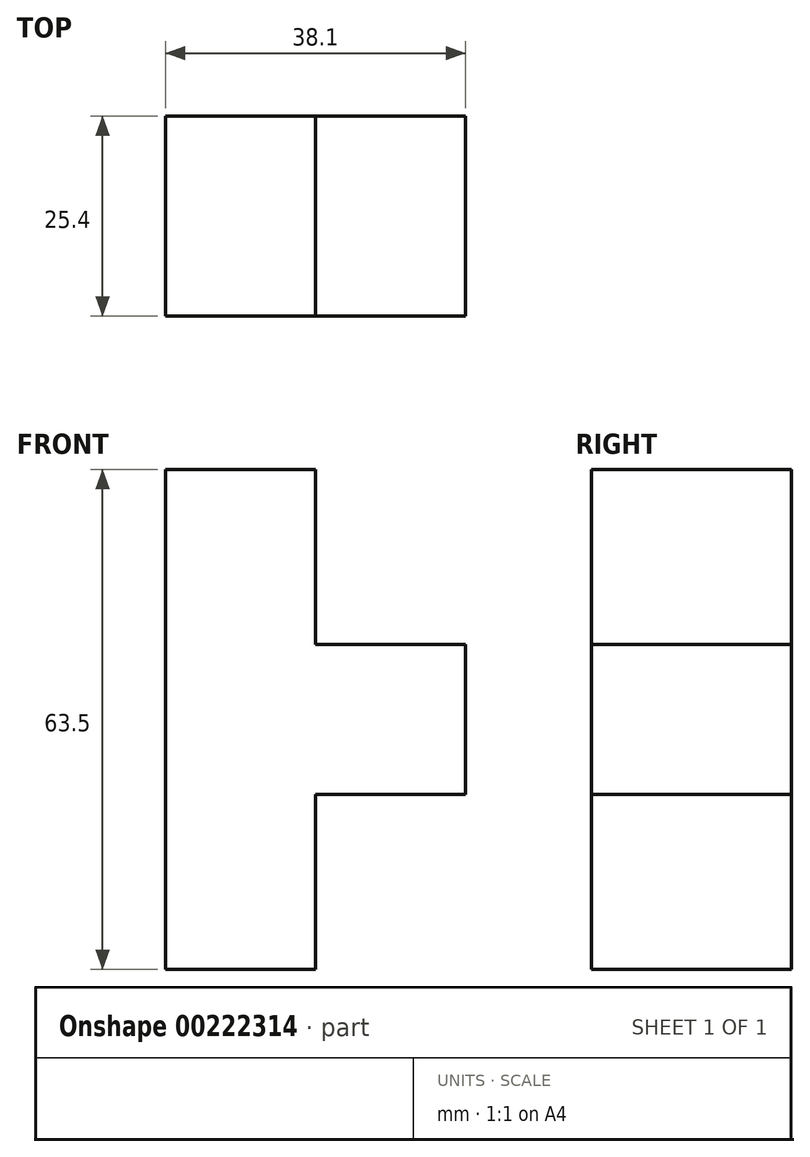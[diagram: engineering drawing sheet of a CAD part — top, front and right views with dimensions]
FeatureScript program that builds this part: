
annotation { "Feature Type Name" : "Feature", "Feature Type Description" : "" }
export const myFeature = defineFeature(function(context is Context, id is Id, definition is map)
    precondition{}
    {
        {
            var Q0;
            Q0=qCreatedBy(makeId("Front.planeOp"),FACE);
            var sketch = newSketch(context, id + "F0", { "sketchPlane" : qUnion([Q0])});
            skLineSegment(sketch, "E0.bottom", {"start": v(-34.1, -0.14) * mm, "end": v(-53.14, -0.14) * mm});
            skLineSegment(sketch, "E0.top", {"start": v(-34.1, 63.36) * mm, "end": v(-53.14, 63.36) * mm});
            skLineSegment(sketch, "E0.left", {"start": v(-34.1, -0.14) * mm, "end": v(-34.1, 63.36) * mm});
            skLineSegment(sketch, "E0.right", {"start": v(-53.14, -0.14) * mm, "end": v(-53.14, 63.36) * mm});
            skPoint(sketch, "E0.middle", {"position": v(-43.62, 31.6) * mm});
            skLineSegment(sketch, "E1.bottom", {"start": v(-34.1, 41.13) * mm, "end": v(-15.04, 41.13) * mm});
            skLineSegment(sketch, "E1.top", {"start": v(-34.1, 22.08) * mm, "end": v(-15.04, 22.08) * mm});
            skLineSegment(sketch, "E1.left", {"start": v(-34.1, 41.13) * mm, "end": v(-34.1, 22.08) * mm});
            skLineSegment(sketch, "E1.right", {"start": v(-15.04, 41.13) * mm, "end": v(-15.04, 22.08) * mm});
            skPoint(sketch, "E1.middle", {"position": v(-24.57, 31.6) * mm});
            skPoint(sketch, "E1.middle.positionSnap0", {"position": v(-34.1, 31.6) * mm});
            skPoint(sketch, "E1.centerSnap0", {"position": v(-34.1, 31.6) * mm});
            skSolve(sketch);
        }
        {
            var Q0;
            Q0=qSketchRegion(id+"F0",true);
            extrude(context, id + "F1", {"entities" : qUnion([Q0]), "endBound" : BoundingType.SYMMETRIC, "depth" : 25.4 * mm});
        }
    });
